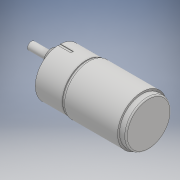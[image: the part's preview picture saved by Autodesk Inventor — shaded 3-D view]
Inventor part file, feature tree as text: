
AUTODESK INVENTOR PART (.ipt)
format: ipt  version: 2017 SP1 (Build 210196100, 196)  size: 167,936 bytes
history: native  units: mm
features: extrude x7, sketch x7, fillet x2, other x1
ambient origin geometry x8: Origin, YZ Plane, XZ Plane, XY Plane, X Axis, Y Axis, Z Axis, Center Point
bodies: Body1 (feature_tree)
feature tree (17):
  other  "Твердое тело1"
  extrude  "Выдавливание1"  Depth=37.0mm
  extrude  "Выдавливание2"  Depth=21.0mm TaperAngle=0.0deg
  extrude  "Выдавливание3"  Depth=30.0mm
  fillet  "Сопряжение1"  Radius=0.2mm
  extrude  "Выдавливание4"  Depth=38.0mm
  fillet  "Сопряжение2"  Radius=43.0mm
  extrude  "Выдавливание5"  Depth=2.0mm
  extrude  "Выдавливание6"  Depth=35.0mm
  extrude  "Выдавливание7"  Depth=5.0mm TaperAngle=0.0deg
  sketch  "Эскиз1"
  sketch  "Эскиз2"
  sketch  "Эскиз3"
  sketch  "Эскиз4"
  sketch  "Эскиз5"
  sketch  "Эскиз6"
  sketch  "Эскиз7"
